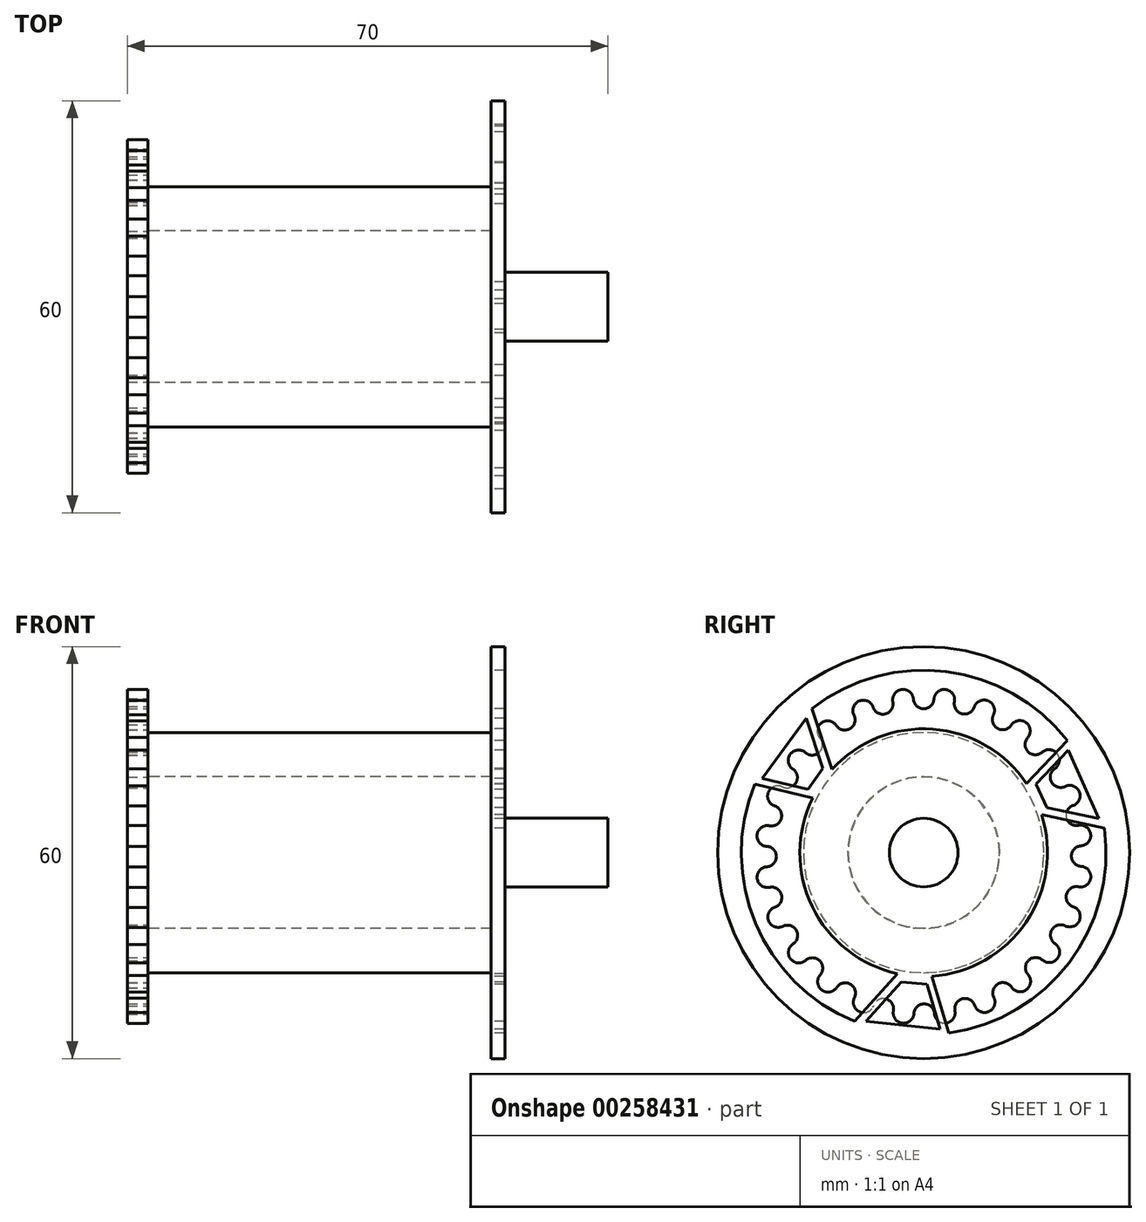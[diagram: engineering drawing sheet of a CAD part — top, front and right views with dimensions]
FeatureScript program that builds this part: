
annotation { "Feature Type Name" : "Feature", "Feature Type Description" : "" }
export const myFeature = defineFeature(function(context is Context, id is Id, definition is map)
    precondition{}
    {
        {
            var Q0;
            Q0=qCreatedBy(makeId("Right.planeOp"),FACE);
            var sketch = newSketch(context, id + "F0", { "sketchPlane" : qUnion([Q0])});
            skCircle(sketch, "E0", {"center": v(0, 0) * mm, "radius": 17.5 * mm});
            skCircle(sketch, "E1", {"center": v(0, 0) * mm, "radius": 11.06 * mm});
            skSolve(sketch);
        }
        {
            var Q0;
            Q0 = qSketchRegion(id + "F0", true);
            extrude(context, id + "F1", {"entities" : qUnion([Q0]), "depth" : 50 * mm});
        }
        {
            var Q0;
            Q0=makeQuery(id+"F1.opExtrude","CAP_FACE",FACE,{"disambiguationData":[OSD([sQuery(id+"F0.wireOp",EDGE,"E0"),sQuery(id+"F0.wireOp",EDGE,"E1")])],"isStart":true});
            var sketch = newSketch(context, id + "F2", { "sketchPlane" : qUnion([Q0])});
            skArc(sketch, "E2", {"start": v(-1.5, 22.45) * mm, "mid": v(0, 20.95) * mm, "end": v(1.5, 22.45) * mm});
            skLineSegment(sketch, "E3", {"start": v(0, 20.95) * mm, "end": v(0, -24.24) * mm, "construction": true});
            skPoint(sketch, "E4.orphan", {"position": v(0, 21.66) * mm});
            skArc(sketch, "E5", {"start": v(4.5, 22.05) * mm, "mid": v(3.2, 23.75) * mm, "end": v(1.5, 22.45) * mm});
            skArc(sketch, "E6.1.0", {"start": v(-1.5, 22.45) * mm, "mid": v(-3.2, 23.76) * mm, "end": v(-4.5, 22.06) * mm});
            skArc(sketch, "E6.1.1", {"start": v(-7.4, 21.29) * mm, "mid": v(-5.56, 20.23) * mm, "end": v(-4.5, 22.06) * mm});
            skArc(sketch, "E6.2.0", {"start": v(-7.4, 21.29) * mm, "mid": v(-9.38, 22.11) * mm, "end": v(-10.2, 20.14) * mm});
            skArc(sketch, "E6.2.1", {"start": v(-12.8, 18.64) * mm, "mid": v(-10.75, 18.09) * mm, "end": v(-10.2, 20.14) * mm});
            skArc(sketch, "E6.3.0", {"start": v(-12.8, 18.64) * mm, "mid": v(-14.92, 18.92) * mm, "end": v(-15.2, 16.8) * mm});
            skArc(sketch, "E6.3.1", {"start": v(-17.33, 14.68) * mm, "mid": v(-15.2, 14.68) * mm, "end": v(-15.2, 16.8) * mm});
            skArc(sketch, "E6.4.0", {"start": v(-17.33, 14.68) * mm, "mid": v(-19.45, 14.4) * mm, "end": v(-19.18, 12.29) * mm});
            skArc(sketch, "E6.4.1", {"start": v(-20.68, 9.69) * mm, "mid": v(-18.63, 10.24) * mm, "end": v(-19.18, 12.29) * mm});
            skArc(sketch, "E6.5.0", {"start": v(-20.68, 9.69) * mm, "mid": v(-22.66, 8.87) * mm, "end": v(-21.84, 6.9) * mm});
            skArc(sketch, "E6.5.1", {"start": v(-22.62, 4) * mm, "mid": v(-20.78, 5.06) * mm, "end": v(-21.84, 6.9) * mm});
            skArc(sketch, "E6.6.0", {"start": v(-22.62, 4) * mm, "mid": v(-24.32, 2.7) * mm, "end": v(-23.03, 1) * mm});
            skArc(sketch, "E6.6.1", {"start": v(-23.03, -2) * mm, "mid": v(-21.53, -0.5) * mm, "end": v(-23.03, 1) * mm});
            skArc(sketch, "E6.7.0", {"start": v(-23.03, -2) * mm, "mid": v(-24.33, -3.7) * mm, "end": v(-22.64, -5) * mm});
            skArc(sketch, "E6.7.1", {"start": v(-21.86, -7.9) * mm, "mid": v(-20.8, -6.07) * mm, "end": v(-22.64, -5) * mm});
            skArc(sketch, "E6.8.0", {"start": v(-21.86, -7.9) * mm, "mid": v(-22.69, -9.88) * mm, "end": v(-20.71, -10.7) * mm});
            skArc(sketch, "E6.8.1", {"start": v(-19.21, -13.3) * mm, "mid": v(-18.67, -11.25) * mm, "end": v(-20.71, -10.7) * mm});
            skArc(sketch, "E6.9.0", {"start": v(-19.21, -13.3) * mm, "mid": v(-19.5, -15.42) * mm, "end": v(-17.38, -15.7) * mm});
            skArc(sketch, "E6.9.1", {"start": v(-15.26, -17.83) * mm, "mid": v(-15.26, -15.7) * mm, "end": v(-17.38, -15.7) * mm});
            skArc(sketch, "E6.10.0", {"start": v(-15.26, -17.83) * mm, "mid": v(-14.98, -19.95) * mm, "end": v(-12.86, -19.68) * mm});
            skArc(sketch, "E6.10.1", {"start": v(-10.26, -21.18) * mm, "mid": v(-10.81, -19.13) * mm, "end": v(-12.86, -19.68) * mm});
            skArc(sketch, "E6.11.0", {"start": v(-10.26, -21.18) * mm, "mid": v(-9.45, -23.16) * mm, "end": v(-7.47, -22.35) * mm});
            skArc(sketch, "E6.11.1", {"start": v(-4.57, -23.12) * mm, "mid": v(-5.63, -21.29) * mm, "end": v(-7.47, -22.35) * mm});
            skArc(sketch, "E6.12.0", {"start": v(-4.57, -23.12) * mm, "mid": v(-3.28, -24.83) * mm, "end": v(-1.57, -23.53) * mm});
            skArc(sketch, "E6.12.1", {"start": v(1.43, -23.53) * mm, "mid": v(-0.07, -22.03) * mm, "end": v(-1.57, -23.53) * mm});
            skArc(sketch, "E6.13.0", {"start": v(1.43, -23.53) * mm, "mid": v(3.12, -24.84) * mm, "end": v(4.43, -23.14) * mm});
            skArc(sketch, "E6.13.1", {"start": v(7.33, -22.37) * mm, "mid": v(5.5, -21.3) * mm, "end": v(4.43, -23.14) * mm});
            skArc(sketch, "E6.14.0", {"start": v(7.33, -22.37) * mm, "mid": v(9.3, -23.2) * mm, "end": v(10.13, -21.22) * mm});
            skArc(sketch, "E6.14.1", {"start": v(12.73, -19.72) * mm, "mid": v(10.68, -19.17) * mm, "end": v(10.13, -21.22) * mm});
            skPoint(sketch, "E6.center", {"position": v(-0.04, -0.54) * mm});
            skArc(sketch, "E7.3.15.0", {"start": v(12.73, -19.72) * mm, "mid": v(14.85, -20) * mm, "end": v(15.13, -17.88) * mm});
            skArc(sketch, "E7.4.15.0", {"start": v(17.25, -15.76) * mm, "mid": v(15.13, -15.76) * mm, "end": v(15.13, -17.88) * mm});
            skArc(sketch, "E7.3.16.0", {"start": v(17.25, -15.76) * mm, "mid": v(19.38, -15.49) * mm, "end": v(19.1, -13.36) * mm});
            skArc(sketch, "E7.4.16.0", {"start": v(20.6, -10.77) * mm, "mid": v(18.56, -11.32) * mm, "end": v(19.1, -13.36) * mm});
            skArc(sketch, "E7.3.17.0", {"start": v(20.6, -10.77) * mm, "mid": v(22.59, -9.95) * mm, "end": v(21.77, -7.97) * mm});
            skArc(sketch, "E7.4.17.0", {"start": v(22.55, -5.08) * mm, "mid": v(20.71, -6.14) * mm, "end": v(21.77, -7.97) * mm});
            skArc(sketch, "E7.3.18.0", {"start": v(22.55, -5.08) * mm, "mid": v(24.25, -3.78) * mm, "end": v(22.95, -2.08) * mm});
            skArc(sketch, "E7.4.18.0", {"start": v(22.95, 0.92) * mm, "mid": v(21.45, -0.58) * mm, "end": v(22.95, -2.08) * mm});
            skArc(sketch, "E7.3.19.0", {"start": v(22.95, 0.92) * mm, "mid": v(24.26, 2.62) * mm, "end": v(22.57, 3.93) * mm});
            skArc(sketch, "E7.4.19.0", {"start": v(21.8, 6.82) * mm, "mid": v(20.73, 4.99) * mm, "end": v(22.57, 3.93) * mm});
            skArc(sketch, "E8.3.20.0", {"start": v(21.8, 6.82) * mm, "mid": v(22.62, 8.8) * mm, "end": v(20.64, 9.62) * mm});
            skArc(sketch, "E8.4.20.0", {"start": v(19.14, 12.22) * mm, "mid": v(18.6, 10.17) * mm, "end": v(20.64, 9.62) * mm});
            skArc(sketch, "E9.3.21.0", {"start": v(19.14, 12.22) * mm, "mid": v(19.43, 14.34) * mm, "end": v(17.3, 14.63) * mm});
            skArc(sketch, "E9.4.21.0", {"start": v(15.18, 16.75) * mm, "mid": v(15.18, 14.63) * mm, "end": v(17.3, 14.63) * mm});
            skArc(sketch, "E9.3.22.0", {"start": v(15.18, 16.75) * mm, "mid": v(14.91, 18.87) * mm, "end": v(12.79, 18.6) * mm});
            skArc(sketch, "E9.4.22.0", {"start": v(10.2, 20.1) * mm, "mid": v(10.74, 18.05) * mm, "end": v(12.79, 18.6) * mm});
            skArc(sketch, "E9.3.23.0", {"start": v(10.2, 20.1) * mm, "mid": v(9.38, 22.08) * mm, "end": v(7.4, 21.27) * mm});
            skArc(sketch, "E9.4.23.0", {"start": v(4.5, 22.05) * mm, "mid": v(5.56, 20.2) * mm, "end": v(7.4, 21.27) * mm});
            skCircle(sketch, "E10", {"center": v(0, 0) * mm, "radius": 11 * mm});
            skSolve(sketch);
        }
        {
            var Q0;
            Q0 = qSketchRegion(id + "F2", true);
            extrude(context, id + "F3", {"entities" : qUnion([Q0]), "operationType" : NewBodyOperationType.ADD, "depth" : 3 * mm});
        }
        {
            var Q0;
            Q0=makeQuery(id+"F1.opExtrude","CAP_FACE",FACE,{"disambiguationData":[OSD([sQuery(id+"F0.wireOp",EDGE,"E0"),sQuery(id+"F0.wireOp",EDGE,"E1")])],"isStart":false});
            var sketch = newSketch(context, id + "F4", { "sketchPlane" : qUnion([Q0])});
            skCircle(sketch, "E11", {"center": v(0, 0) * mm, "radius": 30 * mm});
            skArc(sketch, "E12", {"start": v(3.66, -26.3) * mm, "mid": v(21.17, -16.04) * mm, "end": v(26.31, 3.6) * mm});
            skArc(sketch, "E13", {"start": v(-16.18, 7.97) * mm, "mid": v(-16.24, -7.85) * mm, "end": v(-3.8, -17.63) * mm});
            skLineSegment(sketch, "E14", {"start": v(1.18, -18) * mm, "end": v(3.66, -26.3) * mm});
            skLineSegment(sketch, "E15", {"start": v(-3.8, -17.63) * mm, "end": v(-10.04, -24.58) * mm});
            skLineSegment(sketch, "E16", {"start": v(2.41, -25.73) * mm, "end": v(0.45, -19.16) * mm});
            skLineSegment(sketch, "E17", {"start": v(0.45, -19.16) * mm, "end": v(-3.28, -18.84) * mm});
            skLineSegment(sketch, "E18", {"start": v(-3.28, -18.84) * mm, "end": v(-8.43, -24.58) * mm});
            skLineSegment(sketch, "E19", {"start": v(-8.43, -24.58) * mm, "end": v(2.41, -25.73) * mm});
            skLineSegment(sketch, "E20.1.0", {"start": v(17.17, 5.52) * mm, "end": v(26.31, 3.6) * mm});
            skLineSegment(sketch, "E20.1.1", {"start": v(15, 10.02) * mm, "end": v(20.95, 16.32) * mm});
            skLineSegment(sketch, "E20.2.0", {"start": v(-13.36, 12.11) * mm, "end": v(-16.27, 20.99) * mm});
            skLineSegment(sketch, "E20.2.1", {"start": v(-16.18, 7.97) * mm, "end": v(-24.6, 9.98) * mm});
            skLineSegment(sketch, "E21.1.0", {"start": v(25.5, 5) * mm, "end": v(21.08, 14.96) * mm});
            skLineSegment(sketch, "E21.1.1", {"start": v(17.96, 6.58) * mm, "end": v(25.5, 5) * mm});
            skLineSegment(sketch, "E21.1.2", {"start": v(16.37, 9.97) * mm, "end": v(17.96, 6.58) * mm});
            skLineSegment(sketch, "E21.1.3", {"start": v(21.08, 14.96) * mm, "end": v(16.37, 9.97) * mm});
            skLineSegment(sketch, "E21.2.0", {"start": v(-17.08, 19.59) * mm, "end": v(-23.49, 10.77) * mm});
            skLineSegment(sketch, "E21.2.1", {"start": v(-14.68, 12.26) * mm, "end": v(-17.08, 19.59) * mm});
            skLineSegment(sketch, "E21.2.2", {"start": v(-16.82, 9.19) * mm, "end": v(-14.68, 12.26) * mm});
            skLineSegment(sketch, "E21.2.3", {"start": v(-23.49, 10.77) * mm, "end": v(-16.82, 9.19) * mm});
            skArc(sketch, "E22.trimOffspring", {"start": v(-24.6, 9.98) * mm, "mid": v(-24.47, -10.31) * mm, "end": v(-10.04, -24.58) * mm});
            skArc(sketch, "E23.trimOffspring", {"start": v(15, 10.02) * mm, "mid": v(1.32, 17.99) * mm, "end": v(-13.36, 12.11) * mm});
            skArc(sketch, "E24.trimOffspring", {"start": v(20.95, 16.32) * mm, "mid": v(3.3, 26.35) * mm, "end": v(-16.27, 20.99) * mm});
            skArc(sketch, "E25.trimOffspring", {"start": v(1.18, -18) * mm, "mid": v(14.91, -10.14) * mm, "end": v(17.17, 5.52) * mm});
            skSolve(sketch);
        }
        {
            var Q0;
            Q0 = qSketchRegion(id + "F4", true);
            extrude(context, id + "F5", {"entities" : qUnion([Q0]), "depth" : 2 * mm});
        }
        {
            var Q0;
            Q0=makeQuery(id+"F5.opExtrude","CAP_FACE",FACE,{"disambiguationData":[OSD([sQuery(id+"F4.wireOp",EDGE,"E11"),sQuery(id+"F4.wireOp",EDGE,"E12"),sQuery(id+"F4.wireOp",EDGE,"E13"),sQuery(id+"F4.wireOp",EDGE,"E14"),sQuery(id+"F4.wireOp",EDGE,"E15"),sQuery(id+"F4.wireOp",EDGE,"E16"),sQuery(id+"F4.wireOp",EDGE,"E17"),sQuery(id+"F4.wireOp",EDGE,"E18"),sQuery(id+"F4.wireOp",EDGE,"E19"),sQuery(id+"F4.wireOp",EDGE,"E20.1.0"),sQuery(id+"F4.wireOp",EDGE,"E20.1.1"),sQuery(id+"F4.wireOp",EDGE,"E20.2.0"),sQuery(id+"F4.wireOp",EDGE,"E20.2.1"),sQuery(id+"F4.wireOp",EDGE,"E21.1.0"),sQuery(id+"F4.wireOp",EDGE,"E21.1.1"),sQuery(id+"F4.wireOp",EDGE,"E21.1.2"),sQuery(id+"F4.wireOp",EDGE,"E21.1.3"),sQuery(id+"F4.wireOp",EDGE,"E21.2.0"),sQuery(id+"F4.wireOp",EDGE,"E21.2.1"),sQuery(id+"F4.wireOp",EDGE,"E21.2.2"),sQuery(id+"F4.wireOp",EDGE,"E21.2.3"),sQuery(id+"F4.wireOp",EDGE,"E22.trimOffspring"),sQuery(id+"F4.wireOp",EDGE,"E23.trimOffspring"),sQuery(id+"F4.wireOp",EDGE,"E24.trimOffspring"),sQuery(id+"F4.wireOp",EDGE,"E25.trimOffspring")])],"isStart":false});
            var sketch = newSketch(context, id + "F6", { "sketchPlane" : qUnion([Q0])});
            skCircle(sketch, "E26", {"center": v(0, 0) * mm, "radius": 5 * mm});
            skSolve(sketch);
        }
        {
            var Q0;
            Q0=makeQuery(id+"F6.imprint","IMPRINT",FACE,{"disambiguationData":[TD([[makeQuery(id+"F6.imprint","IMPRINT",EDGE,{"derivedFrom":sQuery(id+"F6.wireOp",EDGE,"E26")}),1.0]])]});
            extrude(context, id + "F7", {"entities" : qUnion([Q0]), "operationType" : NewBodyOperationType.ADD, "depth" : 15 * mm});
        }
    });
